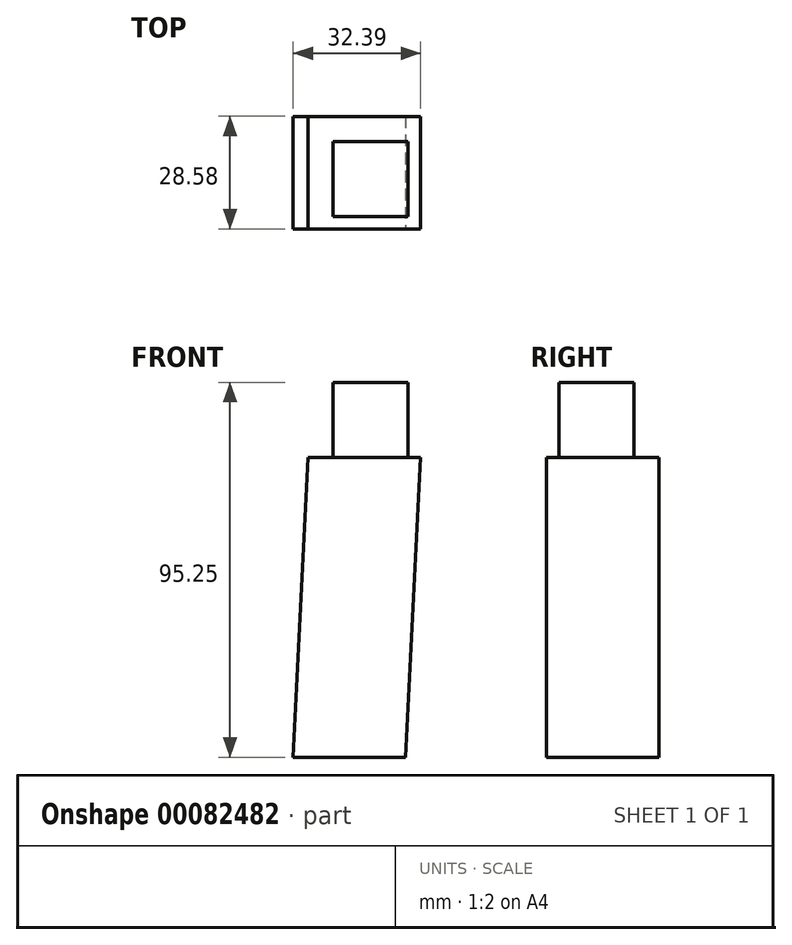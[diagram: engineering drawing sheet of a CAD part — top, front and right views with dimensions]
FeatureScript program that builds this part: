
annotation { "Feature Type Name" : "Feature", "Feature Type Description" : "" }
export const myFeature = defineFeature(function(context is Context, id is Id, definition is map)
    precondition{}
    {
        {
            var Q0;
            Q0=qCreatedBy(makeId("Top.planeOp"),FACE);
            var sketch = newSketch(context, id + "F0", { "sketchPlane" : qUnion([Q0])});
            skLineSegment(sketch, "E0.bottom", {"start": v(14.29, 14.29) * mm, "end": v(-14.29, 14.29) * mm});
            skLineSegment(sketch, "E0.top", {"start": v(14.29, -14.29) * mm, "end": v(-14.29, -14.29) * mm});
            skLineSegment(sketch, "E0.left", {"start": v(14.29, 14.29) * mm, "end": v(14.29, -14.29) * mm});
            skLineSegment(sketch, "E0.right", {"start": v(-14.29, 14.29) * mm, "end": v(-14.29, -14.29) * mm});
            skPoint(sketch, "E0.middle", {"position": v(0, 0) * mm});
            skSolve(sketch);
        }
        {
            var Q0;
            Q0=qCreatedBy(makeId("Front.planeOp"),FACE);
            var sketch = newSketch(context, id + "F1", { "sketchPlane" : qUnion([Q0])});
            skLineSegment(sketch, "E1", {"start": v(0, 0) * mm, "end": v(3.8, 76.2) * mm});
            skSolve(sketch);
        }
        {
            var Q0;
            Q0=qSketchRegion(id+"F0",true);
            var Q1;
            Q1=qConstructionFilter(qBodyType(qCreatedBy(id+"F1",EDGE),BodyType.WIRE),ConstructionObject.NO);
            sweep(context, id + "F2", {"profiles" : qUnion([Q0]), "path" : qUnion([Q1])});
        }
        {
            var Q0;
            Q0=makeQuery(id+"F2.opSweep","CAP_FACE",FACE,{"disambiguationData":[OSD([sQuery(id+"F0.wireOp",EDGE,"E0.bottom"),sQuery(id+"F0.wireOp",EDGE,"E0.top"),sQuery(id+"F0.wireOp",EDGE,"E0.left"),sQuery(id+"F0.wireOp",EDGE,"E0.right"),sQuery(id+"F1.wireOp",VERTEX,"E1.end")])],"isStart":false});
            var sketch = newSketch(context, id + "F3", { "sketchPlane" : qUnion([Q0])});
            skLineSegment(sketch, "E2.bottom", {"start": v(-4.13, 7.94) * mm, "end": v(14.92, 7.94) * mm});
            skLineSegment(sketch, "E2.top", {"start": v(-4.13, -11.11) * mm, "end": v(14.92, -11.11) * mm});
            skLineSegment(sketch, "E2.left", {"start": v(-4.13, 7.94) * mm, "end": v(-4.13, -11.11) * mm});
            skLineSegment(sketch, "E2.right", {"start": v(14.92, 7.94) * mm, "end": v(14.92, -11.11) * mm});
            skSolve(sketch);
        }
        {
            var Q0;
            Q0=qSketchRegion(id+"F3",true);
            extrude(context, id + "F4", {"entities" : qUnion([Q0]), "operationType" : NewBodyOperationType.ADD, "depth" : 19.05 * mm});
        }
    });
